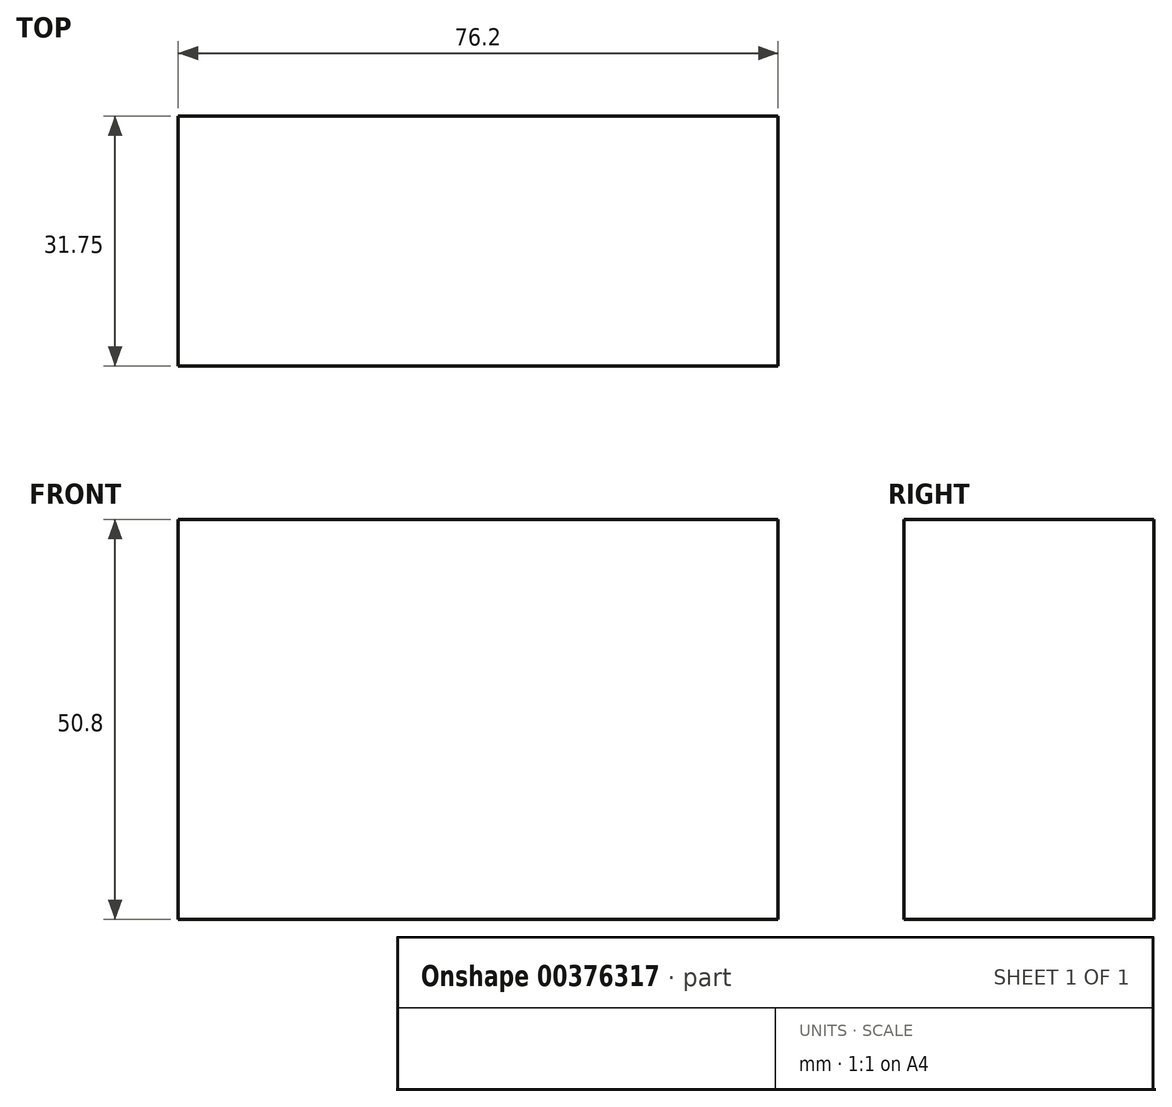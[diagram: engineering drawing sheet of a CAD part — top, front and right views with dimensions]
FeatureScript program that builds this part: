
annotation { "Feature Type Name" : "Feature", "Feature Type Description" : "" }
export const myFeature = defineFeature(function(context is Context, id is Id, definition is map)
    precondition{}
    {
        {
            var Q0;
            Q0=qCreatedBy(makeId("Front.planeOp"),FACE);
            var sketch = newSketch(context, id + "F0", { "sketchPlane" : qUnion([Q0])});
            skLineSegment(sketch, "E0.bottom", {"start": v(10.39, 56.14) * mm, "end": v(-65.81, 56.14) * mm});
            skLineSegment(sketch, "E0.top", {"start": v(10.39, 5.34) * mm, "end": v(-65.81, 5.34) * mm});
            skLineSegment(sketch, "E0.left", {"start": v(10.39, 56.14) * mm, "end": v(10.39, 5.34) * mm});
            skLineSegment(sketch, "E0.right", {"start": v(-65.81, 56.14) * mm, "end": v(-65.81, 5.34) * mm});
            skSolve(sketch);
        }
        {
            var Q0;
            Q0=makeQuery(id+"F0.imprint","IMPRINT",FACE,{"disambiguationData":[TD([[makeQuery(id+"F0.imprint","IMPRINT",EDGE,{"derivedFrom":sQuery(id+"F0.wireOp",EDGE,"E0.bottom")}),1.0]])]});
            extrude(context, id + "F1", {"entities" : qUnion([Q0]), "depth" : 31.75 * mm});
        }
    });
